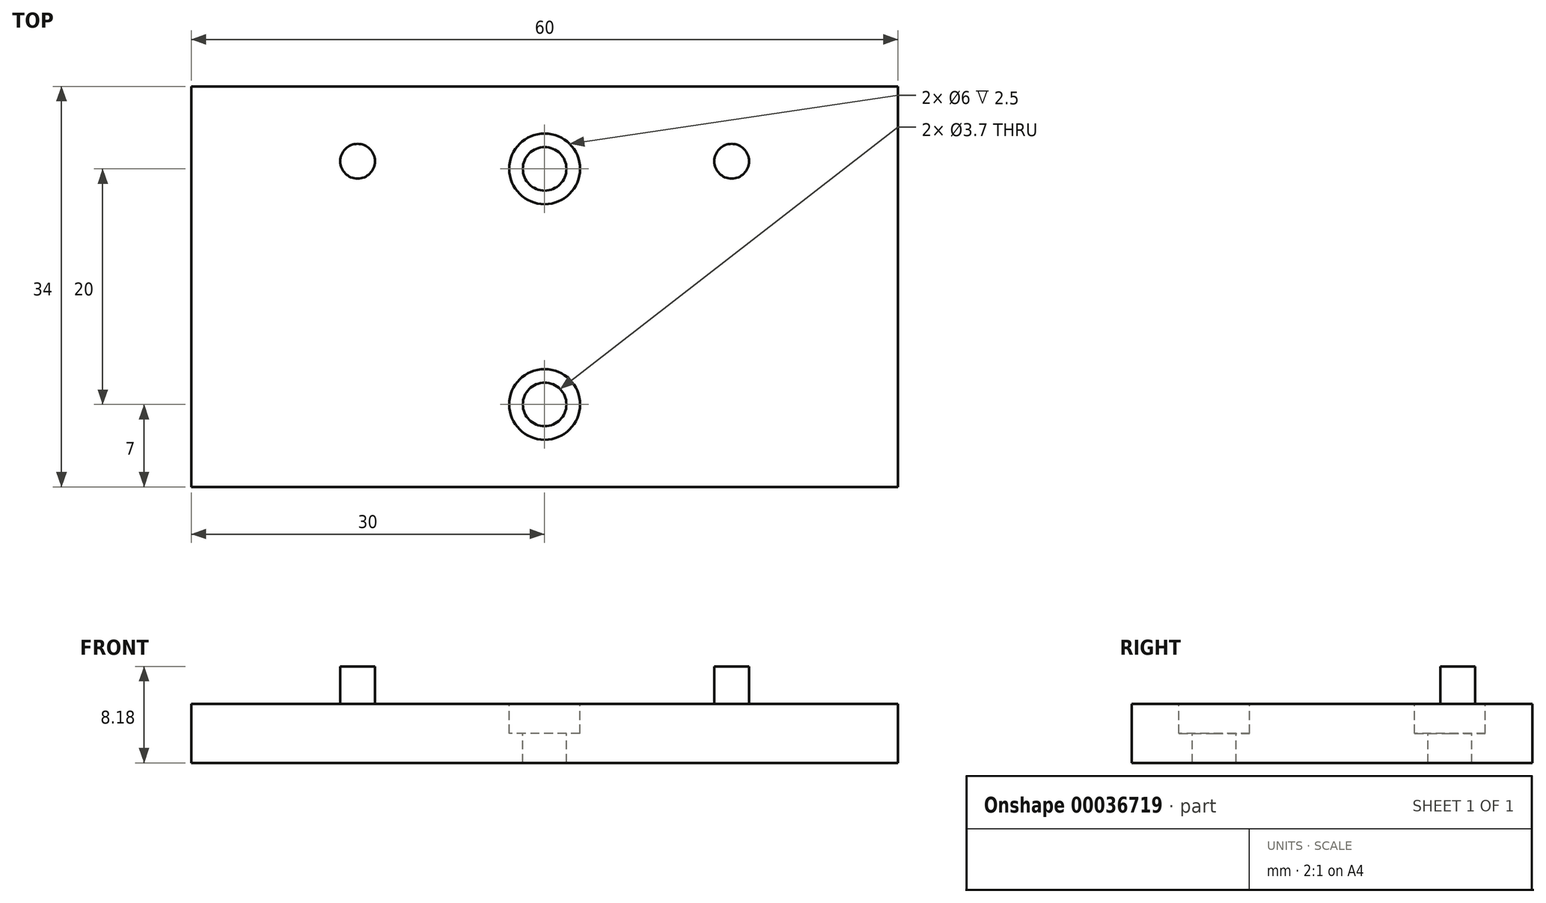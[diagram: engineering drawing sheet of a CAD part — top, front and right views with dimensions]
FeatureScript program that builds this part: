
annotation { "Feature Type Name" : "Feature", "Feature Type Description" : "" }
export const myFeature = defineFeature(function(context is Context, id is Id, definition is map)
    precondition{}
    {
        {
            var Q0;
            Q0=qCreatedBy(makeId("Top.planeOp"),FACE);
            var sketch = newSketch(context, id + "F0", { "sketchPlane" : qUnion([Q0])});
            skLineSegment(sketch, "E0.bottom", {"start": v(30, 17) * mm, "end": v(-30, 17) * mm});
            skLineSegment(sketch, "E0.top", {"start": v(30, -17) * mm, "end": v(-30, -17) * mm});
            skLineSegment(sketch, "E0.left", {"start": v(30, 17) * mm, "end": v(30, -17) * mm});
            skLineSegment(sketch, "E0.right", {"start": v(-30, 17) * mm, "end": v(-30, -17) * mm});
            skPoint(sketch, "E0.middle", {"position": v(0, 0) * mm});
            skSolve(sketch);
        }
        {
            var Q0;
            Q0=makeQuery(id+"F0.imprint","IMPRINT",FACE,{"disambiguationData":[TD([[makeQuery(id+"F0.imprint","IMPRINT",EDGE,{"derivedFrom":sQuery(id+"F0.wireOp",EDGE,"E0.bottom")}),1.0]])]});
            extrude(context, id + "F1", {"entities" : qUnion([Q0]), "depth" : 5 * mm, "offsetDistance" : 25.4 * mm});
        }
        {
            var Q0;
            Q0=makeQuery(id+"F1.opExtrude","CAP_FACE",FACE,{"disambiguationData":[OSD([sQuery(id+"F0.wireOp",EDGE,"E0.bottom"),sQuery(id+"F0.wireOp",EDGE,"E0.top"),sQuery(id+"F0.wireOp",EDGE,"E0.left"),sQuery(id+"F0.wireOp",EDGE,"E0.right")])],"isStart":false});
            var sketch = newSketch(context, id + "F2", { "sketchPlane" : qUnion([Q0])});
            skCircle(sketch, "E1", {"center": v(0, 10) * mm, "radius": 3 * mm});
            skPoint(sketch, "E1.centerSnap0", {"position": v(0, 17) * mm});
            skCircle(sketch, "E2", {"center": v(0, -10) * mm, "radius": 3 * mm});
            skSolve(sketch);
        }
        {
            var Q0;
            Q0=makeQuery(id+"F2.imprint","IMPRINT",FACE,{"disambiguationData":[TD([[makeQuery(id+"F2.imprint","IMPRINT",EDGE,{"derivedFrom":sQuery(id+"F2.wireOp",EDGE,"E1")}),1.0]])]});
            var Q1;
            Q1=makeQuery(id+"F2.imprint","IMPRINT",FACE,{"disambiguationData":[TD([[makeQuery(id+"F2.imprint","IMPRINT",EDGE,{"derivedFrom":sQuery(id+"F2.wireOp",EDGE,"E2")}),1.0]])]});
            var Q2;
            Q2=sQuery(id+"F2.wireOp",EDGE,"E1");
            var Q3;
            Q3=sQuery(id+"F2.wireOp",EDGE,"E2");
            extrude(context, id + "F3", {"entities" : qUnion([Q0, Q1]), "operationType" : NewBodyOperationType.REMOVE, "surfaceEntities" : qUnion([Q2, Q3]), "oppositeDirection" : true, "depth" : 2.5 * mm, "offsetDistance" : 25.4 * mm});
        }
        {
            var Q0;
            Q0=makeQuery(id+"F3.boolean.opBoolean","COPY",FACE,{"derivedFrom":makeQuery(id+"F3.opExtrude","CAP_FACE",FACE,{"disambiguationData":[OSD([sQuery(id+"F2.wireOp",EDGE,"E1")])],"isStart":false})});
            var sketch = newSketch(context, id + "F4", { "sketchPlane" : qUnion([Q0])});
            skCircle(sketch, "E3", {"center": v(0, 10) * mm, "radius": 1.85 * mm});
            skCircle(sketch, "E4", {"center": v(0, -10) * mm, "radius": 1.85 * mm});
            skSolve(sketch);
        }
        {
            var Q0;
            Q0=makeQuery(id+"F4.imprint","IMPRINT",FACE,{"disambiguationData":[TD([[makeQuery(id+"F4.imprint","IMPRINT",EDGE,{"derivedFrom":sQuery(id+"F4.wireOp",EDGE,"E3")}),1.0]])]});
            var Q1;
            Q1=makeQuery(id+"F4.imprint","IMPRINT",FACE,{"disambiguationData":[TD([[makeQuery(id+"F4.imprint","IMPRINT",EDGE,{"derivedFrom":sQuery(id+"F4.wireOp",EDGE,"E4")}),1.0]])]});
            extrude(context, id + "F5", {"entities" : qUnion([Q0, Q1]), "operationType" : NewBodyOperationType.REMOVE, "endBound" : BoundingType.THROUGH_ALL, "oppositeDirection" : true, "depth" : 25.4 * mm, "offsetDistance" : 25.4 * mm});
        }
        {
            var Q0;
            Q0=makeQuery(id+"F1.opExtrude","CAP_FACE",FACE,{"disambiguationData":[OSD([sQuery(id+"F0.wireOp",EDGE,"E0.bottom"),sQuery(id+"F0.wireOp",EDGE,"E0.top"),sQuery(id+"F0.wireOp",EDGE,"E0.left"),sQuery(id+"F0.wireOp",EDGE,"E0.right")])],"isStart":false});
            var sketch = newSketch(context, id + "F6", { "sketchPlane" : qUnion([Q0])});
            skCircle(sketch, "E5", {"center": v(-15.88, 10.65) * mm, "radius": 1.47 * mm});
            skCircle(sketch, "E6", {"center": v(15.88, 10.65) * mm, "radius": 1.47 * mm});
            skSolve(sketch);
        }
        {
            var Q0;
            Q0 = qSketchRegion(id + "F6", true);
            extrude(context, id + "F7", {"entities" : qUnion([Q0]), "operationType" : NewBodyOperationType.ADD, "depth" : 3.17 * mm, "offsetDistance" : 25.4 * mm});
        }
    });
